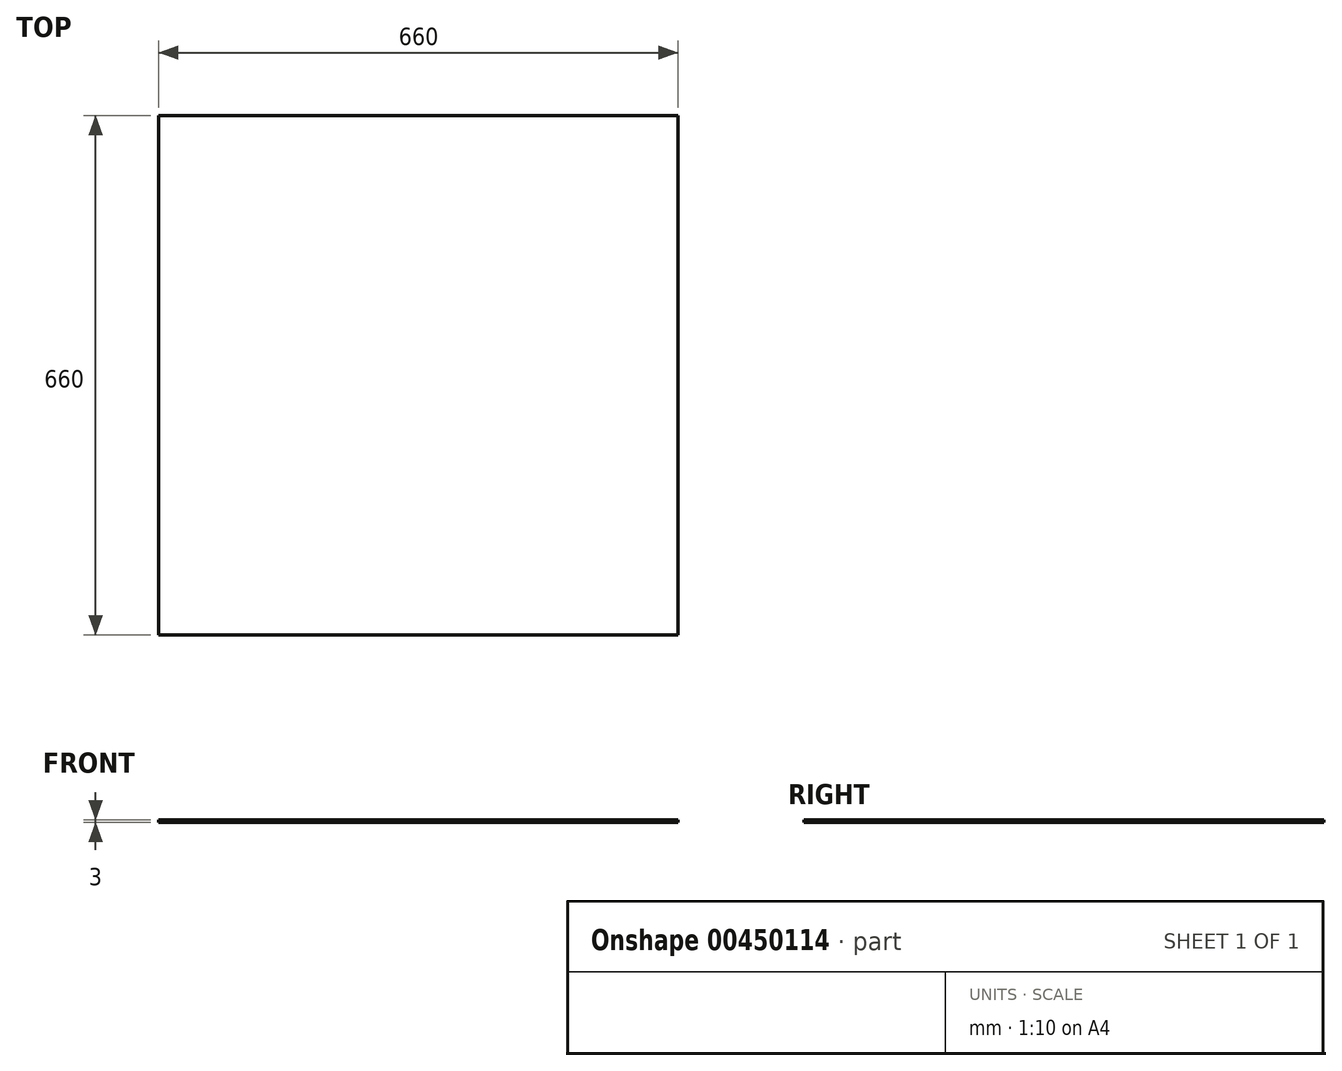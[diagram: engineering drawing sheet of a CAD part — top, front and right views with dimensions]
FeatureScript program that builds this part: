
annotation { "Feature Type Name" : "Feature", "Feature Type Description" : "" }
export const myFeature = defineFeature(function(context is Context, id is Id, definition is map)
    precondition{}
    {
        {
            var Q0;
            Q0=qCreatedBy(makeId("Top.planeOp"),FACE);
            var sketch = newSketch(context, id + "F0", { "sketchPlane" : qUnion([Q0])});
            skLineSegment(sketch, "E0.bottom", {"start": v(245, -250) * mm, "end": v(-245, -250) * mm});
            skLineSegment(sketch, "E0.top", {"start": v(245, 250) * mm, "end": v(-245, 250) * mm});
            skLineSegment(sketch, "E0.left", {"start": v(250, -245) * mm, "end": v(250, 245) * mm});
            skLineSegment(sketch, "E0.right", {"start": v(-250, -245) * mm, "end": v(-250, 245) * mm});
            skPoint(sketch, "E0.middle", {"position": v(0, 0) * mm});
            skPoint(sketch, "E1.visualSharp", {"position": v(-250, 250) * mm});
            skArc(sketch, "E1.filletArc", {"start": v(-245, 250) * mm, "mid": v(-248.54, 248.54) * mm, "end": v(-250, 245) * mm});
            skPoint(sketch, "E2.visualSharp", {"position": v(250, 250) * mm});
            skArc(sketch, "E2.filletArc", {"start": v(250, 245) * mm, "mid": v(248.54, 248.54) * mm, "end": v(245, 250) * mm});
            skPoint(sketch, "E3.visualSharp", {"position": v(250, -250) * mm});
            skArc(sketch, "E3.filletArc", {"start": v(245, -250) * mm, "mid": v(248.54, -248.54) * mm, "end": v(250, -245) * mm});
            skPoint(sketch, "E4.visualSharp", {"position": v(-250, -250) * mm});
            skArc(sketch, "E4.filletArc", {"start": v(-250, -245) * mm, "mid": v(-248.54, -248.54) * mm, "end": v(-245, -250) * mm});
            skLineSegment(sketch, "E5.bottom", {"start": v(330, -330) * mm, "end": v(-330, -330) * mm});
            skLineSegment(sketch, "E5.top", {"start": v(330, 330) * mm, "end": v(-330, 330) * mm});
            skLineSegment(sketch, "E5.left", {"start": v(330, -330) * mm, "end": v(330, 330) * mm});
            skLineSegment(sketch, "E5.right", {"start": v(-330, -330) * mm, "end": v(-330, 330) * mm});
            skPoint(sketch, "E6", {"position": v(330, -330) * mm});
            skSolve(sketch);
        }
        {
            var Q0;
            Q0=makeQuery(id+"F0.imprint","IMPRINT",FACE,{"disambiguationData":[TD([[makeQuery(id+"F0.imprint","IMPRINT",EDGE,{"derivedFrom":sQuery(id+"F0.wireOp",EDGE,"E5.bottom")}),-1.0]])]});
            var Q1;
            Q1=makeQuery(id+"F0.imprint","IMPRINT",FACE,{"disambiguationData":[TD([[makeQuery(id+"F0.imprint","IMPRINT",EDGE,{"derivedFrom":sQuery(id+"F0.wireOp",EDGE,"E0.bottom")}),-1.0]])]});
            extrude(context, id + "F1", {"entities" : qUnion([Q0, Q1]), "depth" : 3 * mm});
        }
        {
            var Q0;
            Q0=makeQuery(id+"F1.opExtrude","CAP_FACE",FACE,{"disambiguationData":[OSD([sQuery(id+"F0.wireOp",EDGE,"E0.bottom"),sQuery(id+"F0.wireOp",EDGE,"E0.top"),sQuery(id+"F0.wireOp",EDGE,"E0.left"),sQuery(id+"F0.wireOp",EDGE,"E0.right"),sQuery(id+"F0.wireOp",EDGE,"E1.filletArc"),sQuery(id+"F0.wireOp",EDGE,"E2.filletArc"),sQuery(id+"F0.wireOp",EDGE,"E3.filletArc"),sQuery(id+"F0.wireOp",EDGE,"E4.filletArc")])],"isStart":true});
            var sketch = newSketch(context, id + "F2", { "sketchPlane" : qUnion([Q0])});
            skLineSegment(sketch, "E7.bottom", {"start": v(230, -230) * mm, "end": v(-230, -230) * mm});
            skLineSegment(sketch, "E7.top", {"start": v(230, 230) * mm, "end": v(-230, 230) * mm});
            skLineSegment(sketch, "E7.left", {"start": v(230, -230) * mm, "end": v(230, 230) * mm});
            skLineSegment(sketch, "E7.right", {"start": v(-230, -230) * mm, "end": v(-230, 230) * mm});
            skPoint(sketch, "E7.middle", {"position": v(0, 0) * mm});
            skSolve(sketch);
        }
    });
